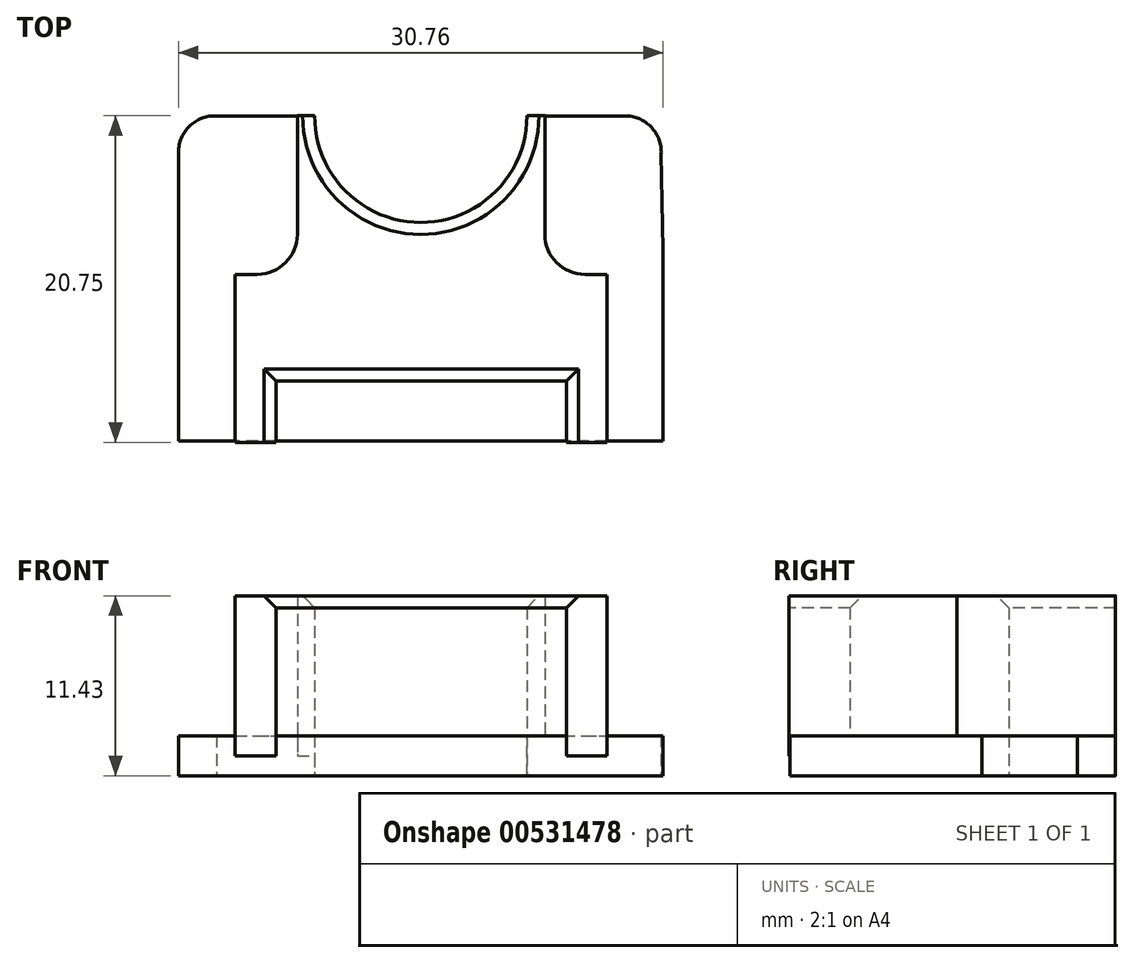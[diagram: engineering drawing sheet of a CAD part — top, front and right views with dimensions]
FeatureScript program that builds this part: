
annotation { "Feature Type Name" : "Feature", "Feature Type Description" : "" }
export const myFeature = defineFeature(function(context is Context, id is Id, definition is map)
    precondition{}
    {
        {
            var Q0;
            Q0=qCreatedBy(makeId("Top.planeOp"),FACE);
            var sketch = newSketch(context, id + "F0", { "sketchPlane" : qUnion([Q0])});
            skLineSegment(sketch, "E0.bottom", {"start": v(15.38, 6.08) * mm, "end": v(-15.38, 6.08) * mm});
            skLineSegment(sketch, "E0.top", {"start": v(15.38, -6.08) * mm, "end": v(-15.38, -6.08) * mm});
            skLineSegment(sketch, "E0.left", {"start": v(15.38, 6.08) * mm, "end": v(15.38, -6.08) * mm});
            skLineSegment(sketch, "E0.right", {"start": v(-15.38, 6.08) * mm, "end": v(-15.38, -6.08) * mm});
            skPoint(sketch, "E0.middle", {"position": v(0, 0) * mm});
            skLineSegment(sketch, "E1", {"start": v(-15.38, 6.08) * mm, "end": v(-15.38, 12.28) * mm});
            skArc(sketch, "E2", {"start": v(-15.38, 12.28) * mm, "mid": v(-14.67, 13.94) * mm, "end": v(-12.98, 14.58) * mm});
            skLineSegment(sketch, "E3", {"start": v(-12.98, 14.58) * mm, "end": v(-6.74, 14.58) * mm});
            skArc(sketch, "E4", {"start": v(-6.74, 14.58) * mm, "mid": v(0, 7.82) * mm, "end": v(6.74, 14.58) * mm});
            skLineSegment(sketch, "E5", {"start": v(6.74, 14.58) * mm, "end": v(12.98, 14.58) * mm});
            skArc(sketch, "E6", {"start": v(12.98, 14.58) * mm, "mid": v(14.64, 13.87) * mm, "end": v(15.27, 12.17) * mm});
            skLineSegment(sketch, "E7", {"start": v(15.27, 12.17) * mm, "end": v(15.38, 6.08) * mm});
            skSolve(sketch);
        }
        {
            var Q0;
            Q0=makeQuery(id+"F0.imprint","IMPRINT",FACE,{"disambiguationData":[TD([[makeQuery(id+"F0.imprint","IMPRINT",EDGE,{"derivedFrom":sQuery(id+"F0.wireOp",EDGE,"E0.bottom")}),1.0]])]});
            var Q1;
            Q1=makeQuery(id+"F0.imprint","IMPRINT",FACE,{"disambiguationData":[TD([[makeQuery(id+"F0.imprint","IMPRINT",EDGE,{"derivedFrom":sQuery(id+"F0.wireOp",EDGE,"E0.bottom")}),-1.0]])]});
            extrude(context, id + "F1", {"entities" : qUnion([Q0, Q1]), "endBound" : BoundingType.SYMMETRIC, "depth" : 2.54 * mm, "offsetDistance" : 25.4 * mm});
        }
        {
            var Q0;
            Q0=qCreatedBy(makeId("Top.planeOp"),FACE);
            var sketch = newSketch(context, id + "F2", { "sketchPlane" : qUnion([Q0])});
            skLineSegment(sketch, "E8", {"start": v(-7.84, 14.81) * mm, "end": v(-7.84, 6.42) * mm});
            skLineSegment(sketch, "E9", {"start": v(-7.84, 6.42) * mm, "end": v(-7.84, 4.51) * mm});
            skLineSegment(sketch, "E10", {"start": v(-7.84, 4.51) * mm, "end": v(-11.79, 4.51) * mm});
            skLineSegment(sketch, "E11", {"start": v(-11.79, 4.51) * mm, "end": v(-11.79, -6.16) * mm});
            skLineSegment(sketch, "E12", {"start": v(-11.79, -6.16) * mm, "end": v(-9.2, -6.16) * mm});
            skLineSegment(sketch, "E13", {"start": v(-9.2, -6.16) * mm, "end": v(-9.2, -2.27) * mm});
            skLineSegment(sketch, "E14", {"start": v(-9.2, -2.27) * mm, "end": v(9.24, -2.27) * mm});
            skLineSegment(sketch, "E15", {"start": v(9.24, -2.27) * mm, "end": v(9.24, -6.16) * mm});
            skLineSegment(sketch, "E16", {"start": v(9.24, -6.16) * mm, "end": v(11.83, -6.16) * mm});
            skLineSegment(sketch, "E17", {"start": v(11.83, -6.16) * mm, "end": v(11.83, 4.51) * mm});
            skLineSegment(sketch, "E18", {"start": v(11.83, 4.51) * mm, "end": v(7.89, 4.51) * mm});
            skLineSegment(sketch, "E19", {"start": v(7.89, 4.51) * mm, "end": v(7.89, 14.75) * mm});
            skArc(sketch, "E20", {"start": v(-6.73, 14.82) * mm, "mid": v(0, 7.81) * mm, "end": v(6.73, 14.82) * mm});
            skLineSegment(sketch, "E21", {"start": v(-7.84, 14.59) * mm, "end": v(-6.74, 14.59) * mm});
            skLineSegment(sketch, "E22", {"start": v(7.89, 14.58) * mm, "end": v(6.74, 14.58) * mm});
            skSolve(sketch);
        }
        {
            var Q0;
            Q0 = qSketchRegion(id + "F2", true);
            var Q1;
            Q1=sQuery(id+"F2.wireOp",EDGE,"E21");
            var Q2;
            Q2=sQuery(id+"F2.wireOp",EDGE,"E20");
            var Q3;
            Q3=sQuery(id+"F2.wireOp",EDGE,"E22");
            var Q4;
            Q4=sQuery(id+"F2.wireOp",EDGE,"E19");
            var Q5;
            Q5=sQuery(id+"F2.wireOp",EDGE,"E18");
            var Q6;
            Q6=sQuery(id+"F2.wireOp",EDGE,"E17");
            var Q7;
            Q7=sQuery(id+"F2.wireOp",EDGE,"E16");
            var Q8;
            Q8=sQuery(id+"F2.wireOp",EDGE,"E14");
            var Q9;
            Q9=sQuery(id+"F2.wireOp",EDGE,"E15");
            var Q10;
            Q10=sQuery(id+"F2.wireOp",EDGE,"E13");
            var Q11;
            Q11=sQuery(id+"F2.wireOp",EDGE,"E12");
            var Q12;
            Q12=sQuery(id+"F2.wireOp",EDGE,"E11");
            var Q13;
            Q13=sQuery(id+"F2.wireOp",EDGE,"E10");
            var Q14;
            Q14=sQuery(id+"F2.wireOp",EDGE,"E9");
            var Q15;
            Q15=sQuery(id+"F2.wireOp",EDGE,"E8");
            extrude(context, id + "F3", {"entities" : qUnion([Q0]), "operationType" : NewBodyOperationType.ADD, "surfaceEntities" : qUnion([Q1, Q2, Q3, Q4, Q5, Q6, Q7, Q8, Q9, Q10, Q11, Q12, Q13, Q14, Q15]), "depth" : 10.16 * mm, "offsetDistance" : 25.4 * mm});
        }
        {
            var Q0;
            Q0=makeQuery(id+"F3.opExtrude","SWEPT_EDGE",EDGE,{"disambiguationData":[OSD([sQuery(id+"F2.wireOp",EDGE,"E18"),sQuery(id+"F2.wireOp",EDGE,"E19")])]});
            var Q1;
            Q1=makeQuery(id+"F3.opExtrude","SWEPT_EDGE",EDGE,{"disambiguationData":[OSD([sQuery(id+"F2.wireOp",EDGE,"E9"),sQuery(id+"F2.wireOp",EDGE,"E10")])]});
            fillet(context, id + "F4", {"entities" : qUnion([Q0, Q1]), "radius" : 2.54 * mm, "tangentPropagation" : true, "allowEdgeOverflow" : false});
        }
        {
            var Q0;
            Q0=makeQuery(id+"F3.opExtrude","CAP_EDGE",EDGE,{"disambiguationData":[OSD([sQuery(id+"F2.wireOp",EDGE,"E20")])],"isStart":false});
            var Q1;
            Q1=makeQuery(id+"F3.opExtrude","CAP_EDGE",EDGE,{"disambiguationData":[OSD([sQuery(id+"F2.wireOp",EDGE,"E14")])],"isStart":false});
            var Q2;
            Q2=makeQuery(id+"F3.opExtrude","CAP_EDGE",EDGE,{"disambiguationData":[OSD([sQuery(id+"F2.wireOp",EDGE,"E15")])],"isStart":false});
            var Q3;
            Q3=makeQuery(id+"F3.opExtrude","CAP_EDGE",EDGE,{"disambiguationData":[OSD([sQuery(id+"F2.wireOp",EDGE,"E13")])],"isStart":false});
            chamfer(context, id + "F5", {"entities" : qUnion([Q0, Q1, Q2, Q3]), "width" : 0.76 * mm, "tangentPropagation" : true});
        }
    });
